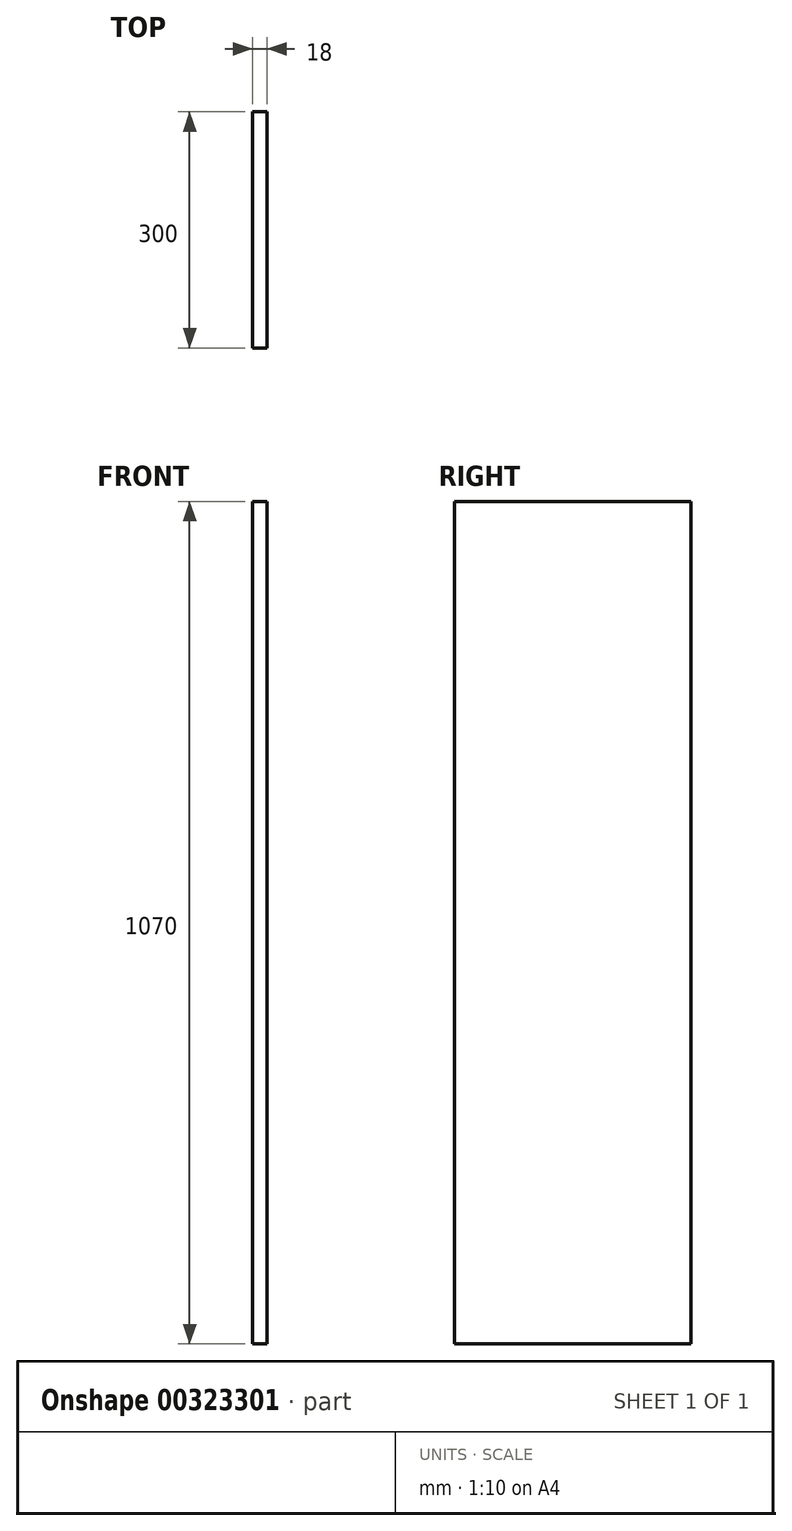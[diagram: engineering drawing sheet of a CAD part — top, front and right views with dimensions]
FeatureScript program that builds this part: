
annotation { "Feature Type Name" : "Feature", "Feature Type Description" : "" }
export const myFeature = defineFeature(function(context is Context, id is Id, definition is map)
    precondition{}
    {
        {
            var Q0;
            Q0=qCreatedBy(makeId("Right.planeOp"),FACE);
            var sketch = newSketch(context, id + "F0", { "sketchPlane" : qUnion([Q0])});
            skLineSegment(sketch, "E0.bottom", {"start": v(0, 0) * mm, "end": v(300, 0) * mm});
            skLineSegment(sketch, "E0.top", {"start": v(0, 1070) * mm, "end": v(300, 1070) * mm});
            skLineSegment(sketch, "E0.left", {"start": v(0, 0) * mm, "end": v(0, 1070) * mm});
            skLineSegment(sketch, "E0.right", {"start": v(300, 0) * mm, "end": v(300, 1070) * mm});
            skSolve(sketch);
        }
        {
            var Q0;
            Q0 = qSketchRegion(id + "F0", true);
            extrude(context, id + "F1", {"entities" : qUnion([Q0]), "depth" : 18 * mm, "offsetDistance" : 25 * mm});
        }
    });
